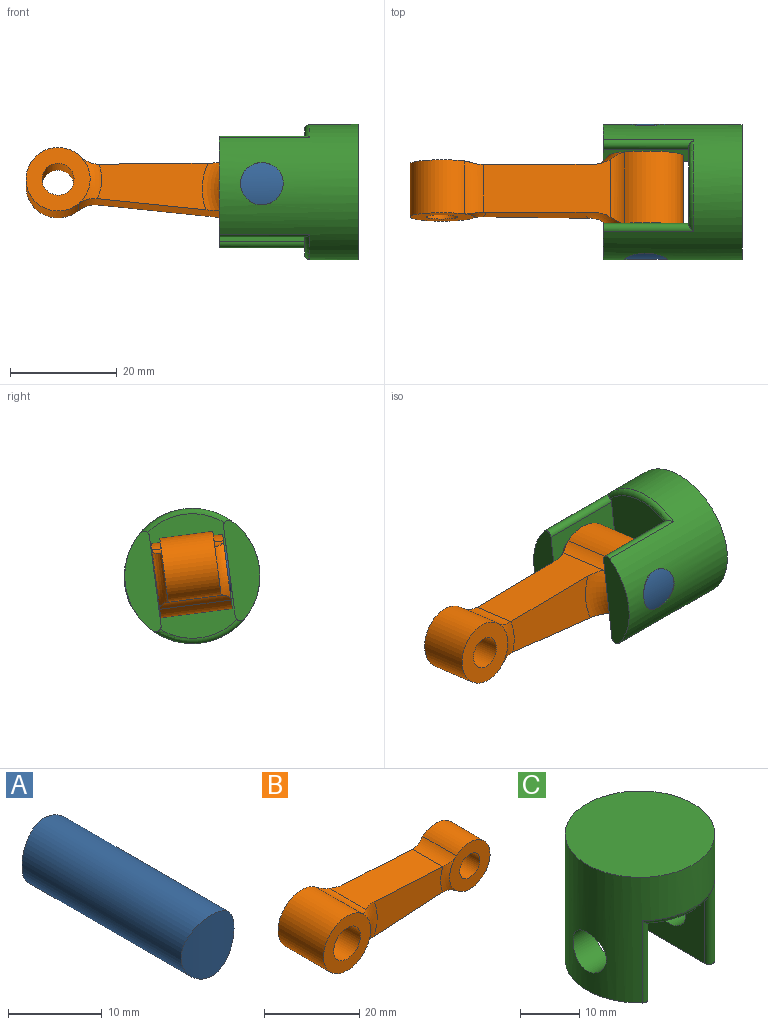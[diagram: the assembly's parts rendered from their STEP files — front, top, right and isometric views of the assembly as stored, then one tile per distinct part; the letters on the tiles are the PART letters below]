
ASSEMBLY  parts=3 mates=2
PART A: 3 faces, bbox 8x25.3x8 mm
  f0: cylinder r=4mm len=25.3mm, axis (0,1,0), area 619.6mm2, adj f1,f2
  f1: cylinder r=12.65mm len=8mm, axis (0,0,1), area 50.9mm2, adj f0
  f2: cylinder r=12.65mm len=8mm, axis (0,0,1), area 50.9mm2, adj f0
PART B: 20 faces, bbox 51.2x19x25.5 mm
  f0: plane 23.7x10.8mm, normal (0.06,0,1), area 215.7mm2, adj f6,f7,f8,f9,f10,f19
  f1: plane 23.7x10.8mm, normal (0.06,0,-1), area 215.7mm2, adj f6,f7,f9,f10,f11,f16
  f2: cylinder r=4mm len=13.5mm, axis (0,1,0), area 339.3mm2, adj f4,f5
  f3: cylinder r=7mm len=14mm, axis (0,1,0), area 418.6mm2, adj f4,f5,f8,f11
  f4: plane 14x14mm, normal (0,-1,0), area 103.7mm2, adj f2,f3,f9
  f5: plane 14x14mm, normal (0,1,0), area 103.7mm2, adj f2,f3,f10
  f6: plane 20.42x8.83mm, normal (0,-1,0), area 148.2mm2, adj f0,f1,f9,f16,f17,f19
  f7: plane 20.42x8.83mm, normal (0,1,0), area 148.2mm2, adj f0,f1,f10,f16,f18,f19
  f8: cylinder r=5mm len=13.5mm, axis (0,1,0), area 36.5mm2, adj f0,f3,f9,f10
  f9: torus R=11.18mm, axis (0,-1,0), area 48.6mm2, adj f0,f1,f4,f6,f8,f11
  f10: torus R=11.18mm, axis (0,-1,0), area 48.6mm2, adj f0,f1,f5,f7,f8,f11
  f11: cylinder r=5mm len=13.5mm, axis (0,1,0), area 36.5mm2, adj f1,f3,f9,f10
  f12: cylinder r=3mm len=10mm, axis (0,1,0), area 188.5mm2, adj f14,f15
  f13: cylinder r=6mm len=12mm, axis (0,1,0), area 275.2mm2, adj f14,f15,f16,f19
  f14: plane 12x12mm, normal (0,-1,0), area 84.8mm2, adj f12,f13,f17
  f15: plane 12x12mm, normal (0,1,0), area 84.8mm2, adj f12,f13,f18
  f16: cylinder r=5mm len=10mm, axis (0,1,0), area 37mm2, adj f1,f6,f7,f13,f17,f18
  f17: torus R=8.18mm, axis (0,-1,0), area 16.5mm2, adj f6,f14,f16,f19
  f18: torus R=8.18mm, axis (0,-1,0), area 16.5mm2, adj f7,f15,f16,f19
  f19: cylinder r=5mm len=10mm, axis (0,1,0), area 37mm2, adj f0,f6,f7,f13,f17,f18
PART C: 15 faces, bbox 25.3x27.4x26 mm
  f0: cylinder r=12.65mm len=26mm, axis (0,0,-1), area 1313.6mm2, adj f1,f2,f3,f7,f8,f9,f10,f11
  f1: plane 18.94x5.65mm, normal (0,0,-1), area 81.8mm2, adj f0,f6,f8,f10
  f2: plane 25.3x25.3mm, normal (0,0,1), area 502.7mm2, adj f0
  f3: plane 18.94x5.65mm, normal (0,0,-1), area 81.8mm2, adj f0,f5,f7,f11
  f4: plane 23.3x14.49mm, normal (0,0,-1), area 305.6mm2, adj f5,f6,f7,f8,f9,f10,f11,f12
  f5: plane 16.94x16mm, normal (-1,0,0), area 220.7mm2, adj f3,f4,f7,f11,f14
  f6: plane 16.94x16mm, normal (1,0,0), area 220.7mm2, adj f1,f4,f8,f10,f13
  f7: cylinder r=1mm len=17mm, axis (0,0,-1), area 37.8mm2, adj f0,f3,f4,f5,f9
  f8: cylinder r=1mm len=17mm, axis (0,0,-1), area 37.8mm2, adj f0,f1,f4,f6,f9
  f9: torus R=11.65mm, axis (0,0,1), area 27.2mm2, adj f0,f4,f7,f8
  f10: cylinder r=1mm len=17mm, axis (0,0,-1), area 37.8mm2, adj f0,f1,f4,f6,f12
  f11: cylinder r=1mm len=17mm, axis (0,0,-1), area 37.8mm2, adj f0,f3,f4,f5,f12
  f12: torus R=11.65mm, axis (0,0,1), area 27.2mm2, adj f0,f4,f10,f11
  f13: cylinder r=4mm len=8mm, axis (1,0,0), area 133.9mm2, adj f0,f6
  f14: cylinder r=4mm len=8mm, axis (1,0,0), area 133.9mm2, adj f0,f5
PLACE A rot(axis=(-0.06,-1,0.06),90.2deg) t=(38.75,20.04,30.34)mm
PLACE B rot(axis=(0,-1,0.06),177.3deg) t=(38.75,20.04,30.34)mm
PLACE C rot(axis=(0.55,0.63,0.55),115.8deg) t=(30.75,19.92,30.36)mm fixed
MATE revolute A.f0 <-> B.f2  axis (0,0.99,-0.13) through (38.75,20.04,30.34)mm
MATE fastened A.f0 <-> C.f13  axis (0,0.99,-0.13) through (38.75,7.34,32)mm
